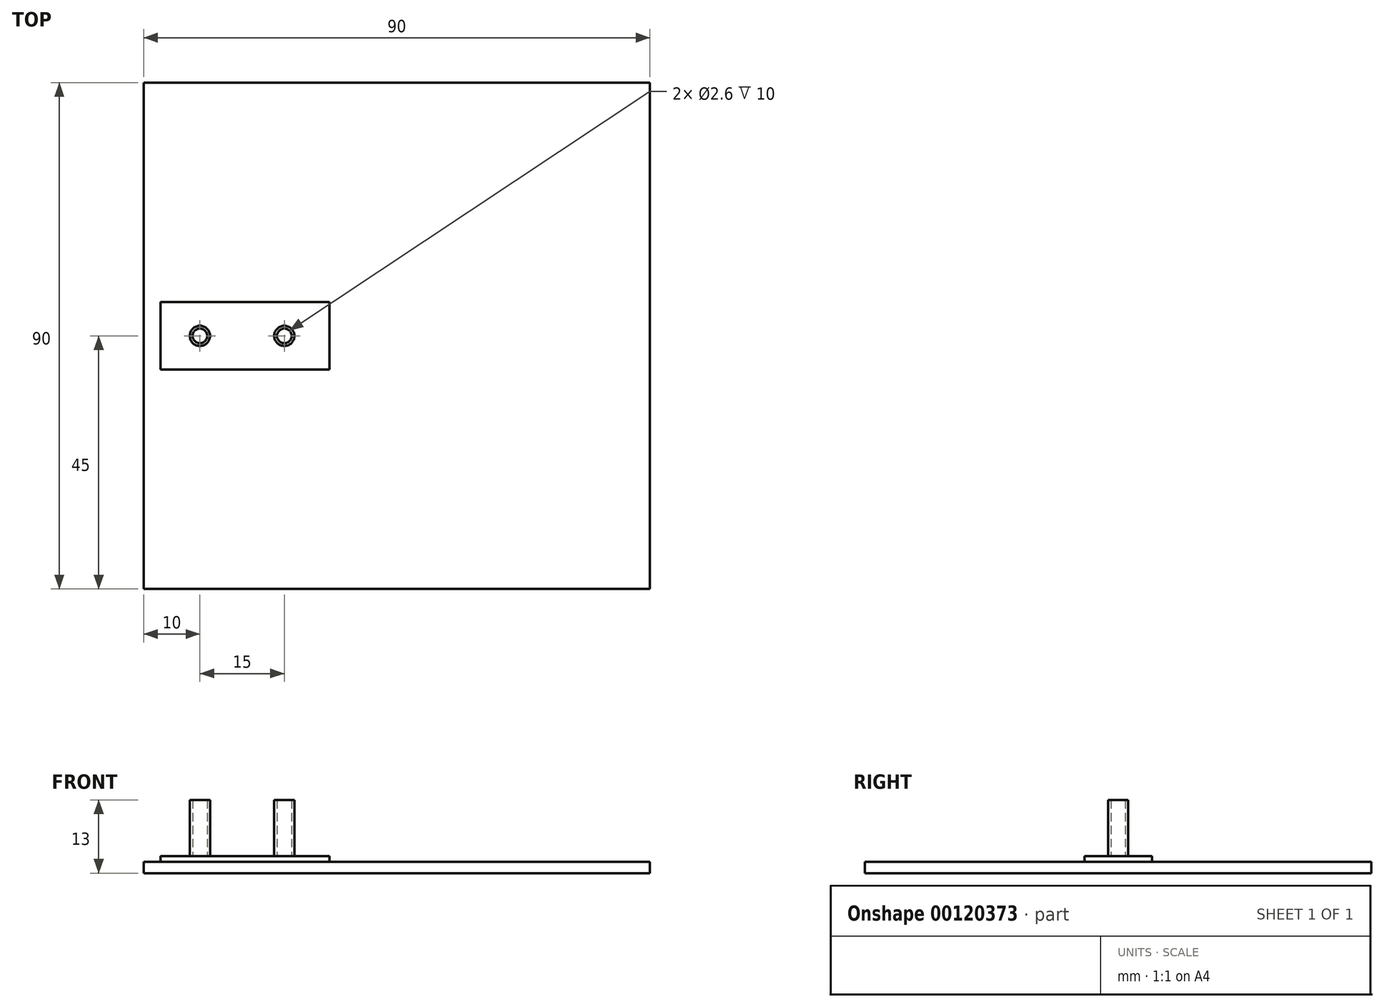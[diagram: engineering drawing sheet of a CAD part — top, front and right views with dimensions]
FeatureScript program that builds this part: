
annotation { "Feature Type Name" : "Feature", "Feature Type Description" : "" }
export const myFeature = defineFeature(function(context is Context, id is Id, definition is map)
    precondition{}
    {
        {
            var Q0;
            Q0=qCreatedBy(makeId("Top.planeOp"),FACE);
            var sketch = newSketch(context, id + "F0", { "sketchPlane" : qUnion([Q0])});
            skLineSegment(sketch, "E0.bottom", {"start": v(-45, 45) * mm, "end": v(45, 45) * mm});
            skLineSegment(sketch, "E0.top", {"start": v(-45, -45) * mm, "end": v(45, -45) * mm});
            skLineSegment(sketch, "E0.left", {"start": v(-45, 45) * mm, "end": v(-45, -45) * mm});
            skLineSegment(sketch, "E0.right", {"start": v(45, 45) * mm, "end": v(45, -45) * mm});
            skLineSegment(sketch, "E1", {"start": v(-45, 0) * mm, "end": v(0, 0) * mm, "construction": true});
            skLineSegment(sketch, "E2", {"start": v(0, 0) * mm, "end": v(45, 0) * mm, "construction": true});
            skCircle(sketch, "E3", {"center": v(-35, 0) * mm, "radius": 1.8 * mm});
            skCircle(sketch, "E4.1.0.0", {"center": v(-20, 0) * mm, "radius": 1.8 * mm});
            skLineSegment(sketch, "E4.direction1", {"start": v(-35, 0) * mm, "end": v(-20, 0) * mm, "construction": true});
            skCircle(sketch, "E5.0", {"center": v(-35, 0) * mm, "radius": 1.3 * mm});
            skCircle(sketch, "E6.1.0.0", {"center": v(-20, 0) * mm, "radius": 1.3 * mm});
            skLineSegment(sketch, "E7.bottom", {"start": v(-42, 6) * mm, "end": v(-12, 6) * mm});
            skLineSegment(sketch, "E7.top", {"start": v(-42, -6) * mm, "end": v(-12, -6) * mm});
            skLineSegment(sketch, "E7.left", {"start": v(-42, 6) * mm, "end": v(-42, -6) * mm});
            skLineSegment(sketch, "E7.right", {"start": v(-12, 6) * mm, "end": v(-12, -6) * mm});
            skLineSegment(sketch, "E8", {"start": v(-35.12, 6) * mm, "end": v(-35.12, 0) * mm, "construction": true});
            skLineSegment(sketch, "E9", {"start": v(-35.12, 0) * mm, "end": v(-35.12, -6) * mm, "construction": true});
            skSolve(sketch);
        }
        {
            var Q0;
            Q0=makeQuery(id+"F0.imprint","IMPRINT",FACE,{"disambiguationData":[TD([[makeQuery(id+"F0.imprint","IMPRINT",EDGE,{"derivedFrom":sQuery(id+"F0.wireOp",EDGE,"E3")}),1.0]])]});
            var Q1;
            Q1=makeQuery(id+"F0.imprint","IMPRINT",FACE,{"disambiguationData":[TD([[makeQuery(id+"F0.imprint","IMPRINT",EDGE,{"derivedFrom":sQuery(id+"F0.wireOp",EDGE,"E4.1.0.0")}),1.0]])]});
            extrude(context, id + "F1", {"entities" : qUnion([Q0, Q1]), "depth" : 13 * mm});
        }
        {
            var Q0;
            Q0=makeQuery(id+"F0.imprint","IMPRINT",FACE,{"disambiguationData":[TD([[makeQuery(id+"F0.imprint","IMPRINT",EDGE,{"derivedFrom":sQuery(id+"F0.wireOp",EDGE,"E6.1.0.0")}),1.0]])]});
            var Q1;
            Q1=makeQuery(id+"F0.imprint","IMPRINT",FACE,{"disambiguationData":[TD([[makeQuery(id+"F0.imprint","IMPRINT",EDGE,{"derivedFrom":sQuery(id+"F0.wireOp",EDGE,"E5.0")}),1.0]])]});
            var Q2;
            Q2=makeQuery(id+"F0.imprint","IMPRINT",FACE,{"disambiguationData":[TD([[makeQuery(id+"F0.imprint","IMPRINT",EDGE,{"derivedFrom":sQuery(id+"F0.wireOp",EDGE,"E3")}),-1.0]])]});
            extrude(context, id + "F2", {"entities" : qUnion([Q0, Q1, Q2]), "operationType" : NewBodyOperationType.ADD, "depth" : 3 * mm});
        }
        {
            var Q0;
            Q0=makeQuery(id+"F0.imprint","IMPRINT",FACE,{"disambiguationData":[TD([[makeQuery(id+"F0.imprint","IMPRINT",EDGE,{"derivedFrom":sQuery(id+"F0.wireOp",EDGE,"E0.bottom")}),-1.0]])]});
            extrude(context, id + "F3", {"entities" : qUnion([Q0]), "operationType" : NewBodyOperationType.ADD, "depth" : 2 * mm});
        }
    });
